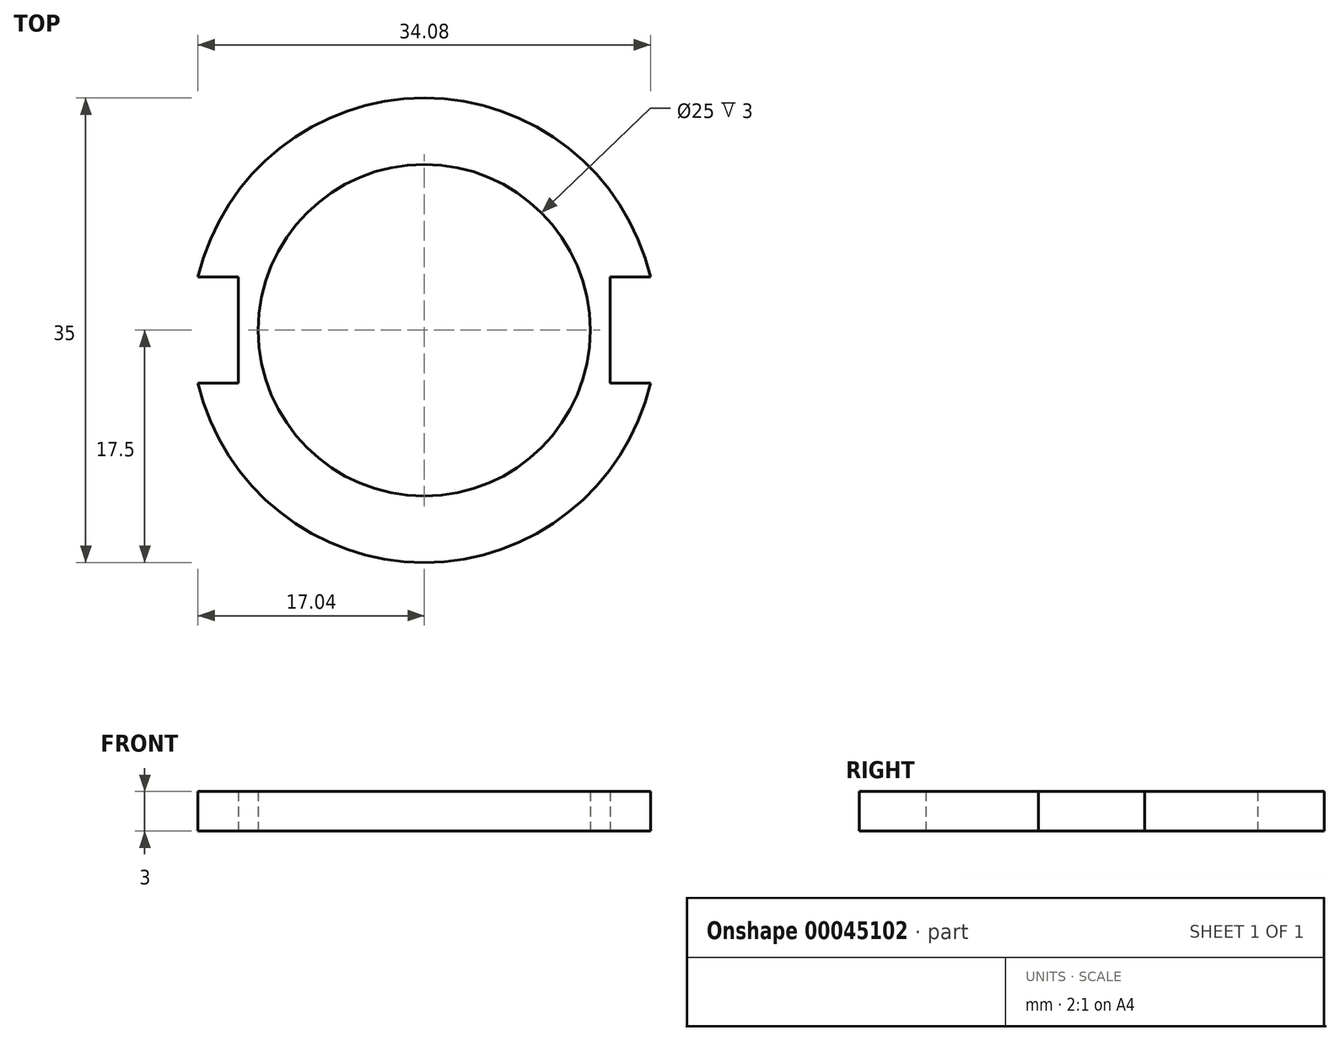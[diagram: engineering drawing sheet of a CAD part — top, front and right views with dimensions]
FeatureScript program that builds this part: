
annotation { "Feature Type Name" : "Feature", "Feature Type Description" : "" }
export const myFeature = defineFeature(function(context is Context, id is Id, definition is map)
    precondition{}
    {
        {
            var Q0;
            Q0=qCreatedBy(makeId("Top.planeOp"),FACE);
            var sketch = newSketch(context, id + "F0", { "sketchPlane" : qUnion([Q0])});
            skArc(sketch, "E0", {"start": v(-17.04, -4) * mm, "mid": v(0, -17.5) * mm, "end": v(17.04, -4) * mm});
            skCircle(sketch, "E1", {"center": v(0, 0) * mm, "radius": 12.5 * mm});
            skLineSegment(sketch, "E2", {"start": v(-17.04, 4) * mm, "end": v(-14, 4) * mm});
            skLineSegment(sketch, "E3", {"start": v(-14, 4) * mm, "end": v(-14, -4) * mm});
            skLineSegment(sketch, "E4", {"start": v(-14, -4) * mm, "end": v(-17.04, -4) * mm});
            skLineSegment(sketch, "E5", {"start": v(17.04, 4) * mm, "end": v(14, 4) * mm});
            skLineSegment(sketch, "E6", {"start": v(14, 4) * mm, "end": v(14, -4) * mm});
            skLineSegment(sketch, "E7", {"start": v(14, -4) * mm, "end": v(17.04, -4) * mm});
            skArc(sketch, "E8.trimOffspring", {"start": v(17.04, 4) * mm, "mid": v(0, 17.5) * mm, "end": v(-17.04, 4) * mm});
            skSolve(sketch);
        }
        {
            var Q0;
            Q0 = qSketchRegion(id + "F0", true);
            var Q1;
            Q1=makeQuery(id+"F0.imprint","IMPRINT",FACE,{"disambiguationData":[TD([[makeQuery(id+"F0.imprint","IMPRINT",EDGE,{"derivedFrom":sQuery(id+"F0.wireOp",EDGE,"E0")}),1.0]])]});
            extrude(context, id + "F1", {"entities" : qUnion([Q0, Q1]), "depth" : 3 * mm});
        }
    });
